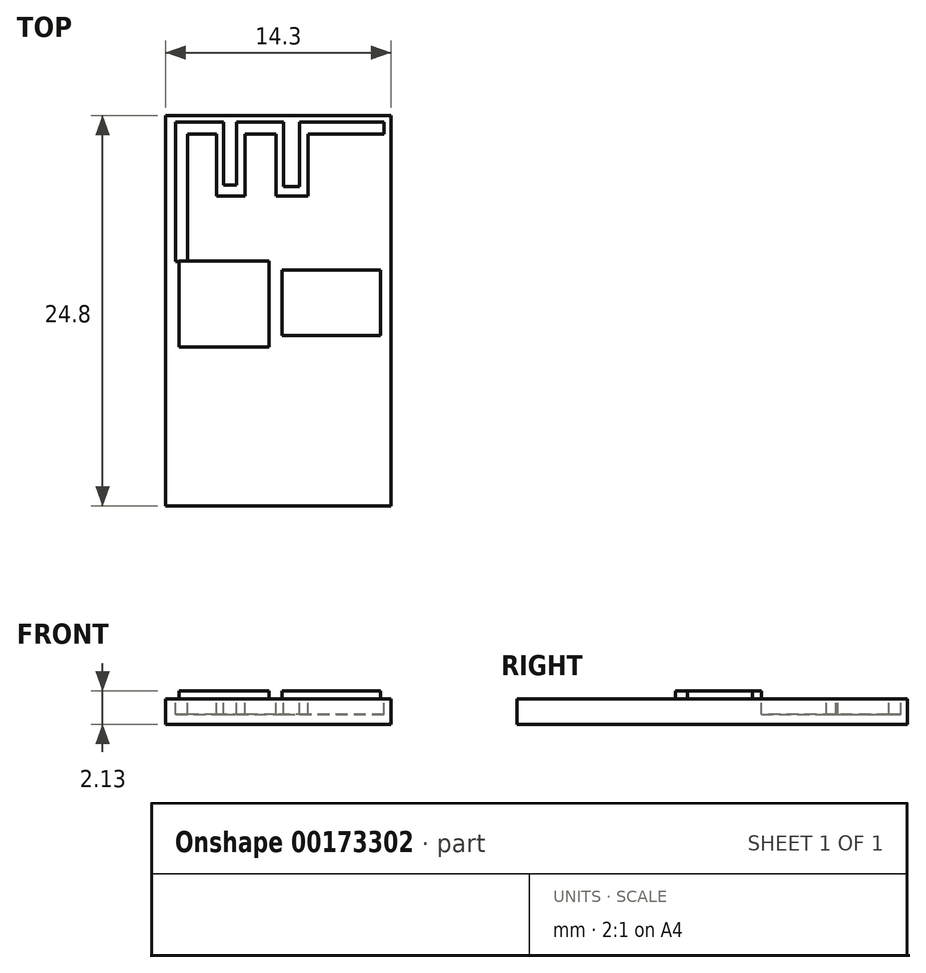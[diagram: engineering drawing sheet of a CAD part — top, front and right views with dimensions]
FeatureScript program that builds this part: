
annotation { "Feature Type Name" : "Feature", "Feature Type Description" : "" }
export const myFeature = defineFeature(function(context is Context, id is Id, definition is map)
    precondition{}
    {
        {
            var Q0;
            Q0=qCreatedBy(makeId("Top.planeOp"),FACE);
            var sketch = newSketch(context, id + "F0", { "sketchPlane" : qUnion([Q0])});
            skLineSegment(sketch, "E0.bottom", {"start": v(-7.15, 12.4) * mm, "end": v(7.15, 12.4) * mm});
            skLineSegment(sketch, "E0.top", {"start": v(-7.15, -12.4) * mm, "end": v(7.15, -12.4) * mm});
            skLineSegment(sketch, "E0.left", {"start": v(-7.15, 12.4) * mm, "end": v(-7.15, -12.4) * mm});
            skLineSegment(sketch, "E0.right", {"start": v(7.15, 12.4) * mm, "end": v(7.15, -12.4) * mm});
            skSolve(sketch);
        }
        {
            var Q0;
            Q0 = qSketchRegion(id + "F0", true);
            extrude(context, id + "F1", {"entities" : qUnion([Q0]), "depth" : 1.63 * mm});
        }
        {
            var Q0;
            Q0=makeQuery(id+"F1.opExtrude","CAP_FACE",FACE,{"disambiguationData":[OSD([sQuery(id+"F0.wireOp",EDGE,"E0.bottom"),sQuery(id+"F0.wireOp",EDGE,"E0.top"),sQuery(id+"F0.wireOp",EDGE,"E0.left"),sQuery(id+"F0.wireOp",EDGE,"E0.right")])],"isStart":false});
            var sketch = newSketch(context, id + "F2", { "sketchPlane" : qUnion([Q0])});
            skLineSegment(sketch, "E1", {"start": v(6.7, 11.23) * mm, "end": v(1.88, 11.23) * mm});
            skLineSegment(sketch, "E2", {"start": v(1.88, 11.23) * mm, "end": v(1.88, 7.27) * mm});
            skLineSegment(sketch, "E3", {"start": v(1.88, 7.27) * mm, "end": v(-0.16, 7.27) * mm});
            skLineSegment(sketch, "E4", {"start": v(-0.16, 7.27) * mm, "end": v(-0.16, 11.23) * mm});
            skLineSegment(sketch, "E5", {"start": v(-0.16, 11.23) * mm, "end": v(-2.11, 11.23) * mm});
            skLineSegment(sketch, "E6", {"start": v(-2.11, 11.23) * mm, "end": v(-2.11, 7.27) * mm});
            skLineSegment(sketch, "E7", {"start": v(-2.11, 7.27) * mm, "end": v(-3.92, 7.27) * mm});
            skLineSegment(sketch, "E8", {"start": v(-3.92, 7.27) * mm, "end": v(-3.92, 11.23) * mm});
            skLineSegment(sketch, "E9", {"start": v(-3.92, 11.23) * mm, "end": v(-5.77, 11.23) * mm});
            skLineSegment(sketch, "E10", {"start": v(-5.77, 11.23) * mm, "end": v(-5.77, 3.13) * mm});
            skLineSegment(sketch, "E11", {"start": v(-5.77, 3.13) * mm, "end": v(-6.52, 3.13) * mm});
            skLineSegment(sketch, "E12", {"start": v(-6.52, 3.13) * mm, "end": v(-6.52, 11.98) * mm});
            skLineSegment(sketch, "E13", {"start": v(-6.52, 11.98) * mm, "end": v(-3.47, 11.98) * mm});
            skLineSegment(sketch, "E14", {"start": v(-3.47, 11.98) * mm, "end": v(-3.47, 7.99) * mm});
            skLineSegment(sketch, "E15", {"start": v(-3.47, 7.99) * mm, "end": v(-2.64, 7.99) * mm});
            skLineSegment(sketch, "E16", {"start": v(-2.64, 7.99) * mm, "end": v(-2.64, 11.98) * mm});
            skLineSegment(sketch, "E17", {"start": v(-2.64, 11.98) * mm, "end": v(0.33, 11.98) * mm});
            skLineSegment(sketch, "E18", {"start": v(0.33, 7.88) * mm, "end": v(1.35, 7.88) * mm});
            skLineSegment(sketch, "E19", {"start": v(1.35, 7.88) * mm, "end": v(1.35, 11.98) * mm});
            skLineSegment(sketch, "E20", {"start": v(1.35, 11.98) * mm, "end": v(6.7, 11.98) * mm});
            skLineSegment(sketch, "E21", {"start": v(6.7, 11.98) * mm, "end": v(6.7, 11.23) * mm});
            skLineSegment(sketch, "E22", {"start": v(0.33, 11.98) * mm, "end": v(0.33, 7.88) * mm});
            skSolve(sketch);
        }
        {
            var Q0;
            Q0 = qSketchRegion(id + "F2", true);
            extrude(context, id + "F3", {"entities" : qUnion([Q0]), "operationType" : NewBodyOperationType.REMOVE, "oppositeDirection" : true, "depth" : 1 * mm});
        }
        {
            var Q0;
            Q0 = qSketchRegion(id + "F2", true);
            extrude(context, id + "F4", {"entities" : qUnion([Q0]), "oppositeDirection" : true, "depth" : 1 * mm});
        }
        {
            var Q0;
            Q0=makeQuery(id+"F1.opExtrude","CAP_FACE",FACE,{"disambiguationData":[OSD([sQuery(id+"F0.wireOp",EDGE,"E0.bottom"),sQuery(id+"F0.wireOp",EDGE,"E0.top"),sQuery(id+"F0.wireOp",EDGE,"E0.left"),sQuery(id+"F0.wireOp",EDGE,"E0.right")])],"isStart":false});
            var sketch = newSketch(context, id + "F5", { "sketchPlane" : qUnion([Q0])});
            skLineSegment(sketch, "E23.bottom", {"start": v(-6.3, 3.14) * mm, "end": v(-0.59, 3.14) * mm});
            skLineSegment(sketch, "E23.top", {"start": v(-6.3, -2.31) * mm, "end": v(-0.59, -2.31) * mm});
            skLineSegment(sketch, "E23.left", {"start": v(-6.3, 3.14) * mm, "end": v(-6.3, -2.31) * mm});
            skLineSegment(sketch, "E23.right", {"start": v(-0.59, 3.14) * mm, "end": v(-0.59, -2.31) * mm});
            skLineSegment(sketch, "E24.bottom", {"start": v(0.23, 2.57) * mm, "end": v(6.49, 2.57) * mm});
            skLineSegment(sketch, "E24.top", {"start": v(0.23, -1.58) * mm, "end": v(6.49, -1.58) * mm});
            skLineSegment(sketch, "E24.left", {"start": v(0.23, 2.57) * mm, "end": v(0.23, -1.58) * mm});
            skLineSegment(sketch, "E24.right", {"start": v(6.49, 2.57) * mm, "end": v(6.49, -1.58) * mm});
            skSolve(sketch);
        }
        {
            var Q0;
            Q0 = qSketchRegion(id + "F5", true);
            extrude(context, id + "F6", {"entities" : qUnion([Q0]), "depth" : .5 * mm});
        }
    });
